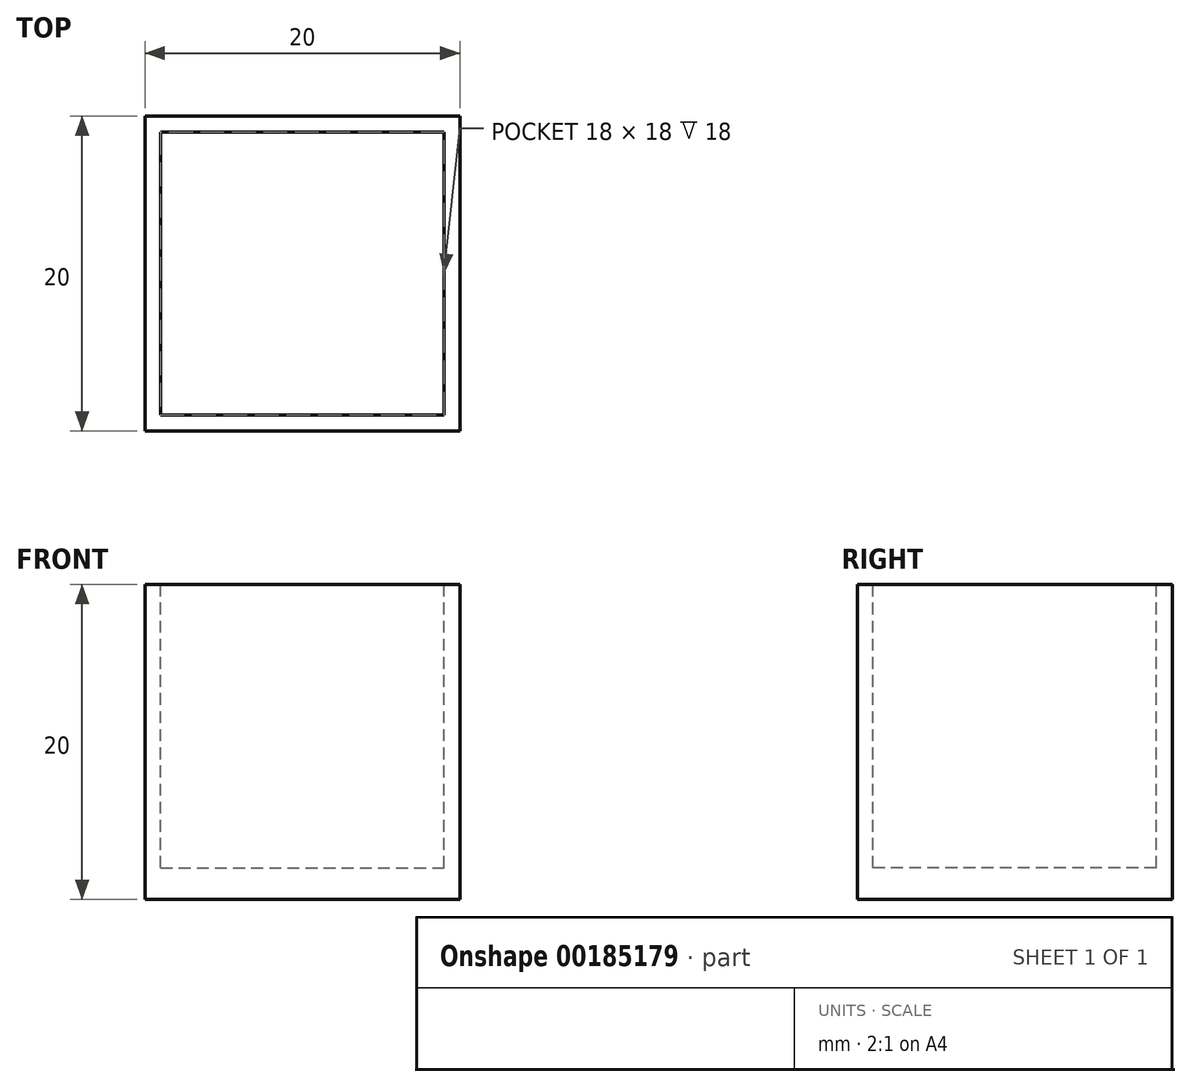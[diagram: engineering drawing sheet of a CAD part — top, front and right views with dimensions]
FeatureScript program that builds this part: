
annotation { "Feature Type Name" : "Feature", "Feature Type Description" : "" }
export const myFeature = defineFeature(function(context is Context, id is Id, definition is map)
    precondition{}
    {
        {
            var Q0;
            Q0=qCreatedBy(makeId("Top.planeOp"),FACE);
            var sketch = newSketch(context, id + "F0", { "sketchPlane" : qUnion([Q0])});
            skLineSegment(sketch, "E0.bottom", {"start": v(10, 10) * mm, "end": v(-10, 10) * mm});
            skLineSegment(sketch, "E0.top", {"start": v(10, -10) * mm, "end": v(-10, -10) * mm});
            skLineSegment(sketch, "E0.left", {"start": v(10, 10) * mm, "end": v(10, -10) * mm});
            skLineSegment(sketch, "E0.right", {"start": v(-10, 10) * mm, "end": v(-10, -10) * mm});
            skPoint(sketch, "E0.middle", {"position": v(0, 0) * mm});
            skSolve(sketch);
        }
        {
            var Q0;
            Q0=makeQuery(id+"F0.imprint","IMPRINT",FACE,{"disambiguationData":[TD([[makeQuery(id+"F0.imprint","IMPRINT",EDGE,{"derivedFrom":sQuery(id+"F0.wireOp",EDGE,"E0.bottom")}),1.0]])]});
            extrude(context, id + "F1", {"entities" : qUnion([Q0]), "depth" : 20 * mm});
        }
        {
            var Q0;
            Q0=makeQuery(id+"F1.opExtrude","CAP_FACE",FACE,{"disambiguationData":[OSD([sQuery(id+"F0.wireOp",EDGE,"E0.bottom"),sQuery(id+"F0.wireOp",EDGE,"E0.top"),sQuery(id+"F0.wireOp",EDGE,"E0.left"),sQuery(id+"F0.wireOp",EDGE,"E0.right")])],"isStart":false});
            var sketch = newSketch(context, id + "F2", { "sketchPlane" : qUnion([Q0])});
            skCircle(sketch, "E1.cCircle", {"center": v(0, 0) * mm, "radius": 9 * mm, "construction": true});
            skLineSegment(sketch, "E1.0", {"start": v(9, 9) * mm, "end": v(9, -9) * mm});
            skLineSegment(sketch, "E1.1", {"start": v(9, -9) * mm, "end": v(-9, -9) * mm});
            skLineSegment(sketch, "E1.2", {"start": v(-9, -9) * mm, "end": v(-9, 9) * mm});
            skLineSegment(sketch, "E1.3", {"start": v(-9, 9) * mm, "end": v(9, 9) * mm});
            skPoint(sketch, "E1.0.midPoint", {"position": v(9, 0) * mm});
            skSolve(sketch);
        }
        {
            var Q0;
            Q0 = qSketchRegion(id + "F2", true);
            extrude(context, id + "F3", {"entities" : qUnion([Q0]), "operationType" : NewBodyOperationType.REMOVE, "oppositeDirection" : true, "depth" : 18 * mm});
        }
    });
